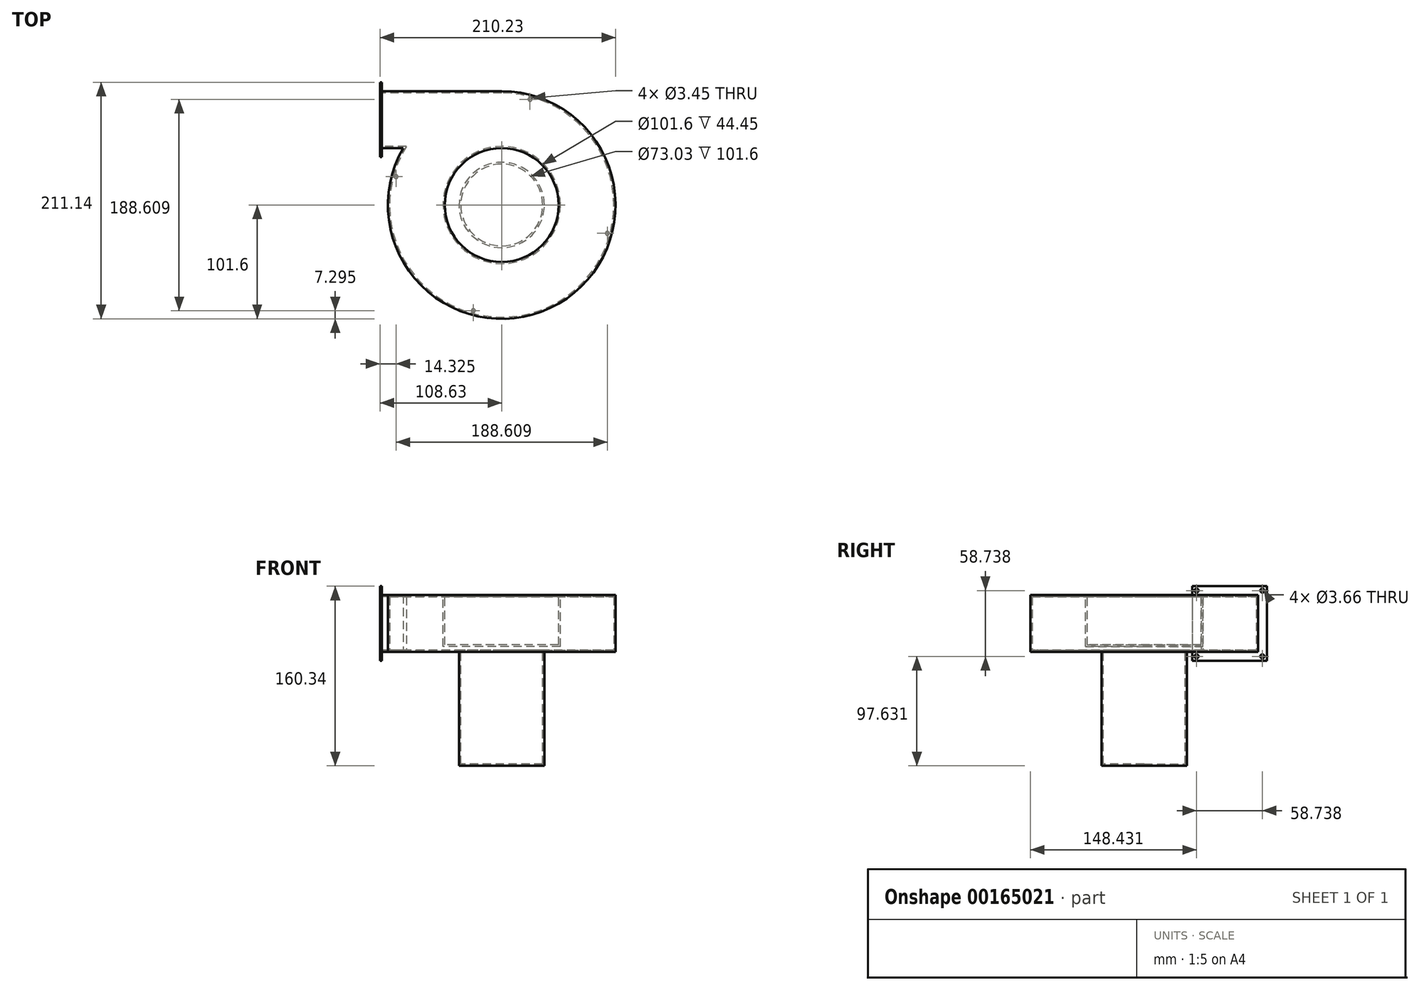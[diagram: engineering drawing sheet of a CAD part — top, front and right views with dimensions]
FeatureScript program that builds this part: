
annotation { "Feature Type Name" : "Feature", "Feature Type Description" : "" }
export const myFeature = defineFeature(function(context is Context, id is Id, definition is map)
    precondition{}
    {
        {
            var Q0;
            Q0=qCreatedBy(makeId("Top.planeOp"),FACE);
            var sketch = newSketch(context, id + "F0", { "sketchPlane" : qUnion([Q0])});
            skLineSegment(sketch, "E0.bottom", {"start": v(-87.99, 50.8) * mm, "end": v(-107.04, 50.8) * mm});
            skLineSegment(sketch, "E0.top", {"start": v(0, 101.6) * mm, "end": v(-107.04, 101.6) * mm});
            skLineSegment(sketch, "E1.top", {"start": v(-107.04, 42.86) * mm, "end": v(-108.63, 42.86) * mm});
            skLineSegment(sketch, "E1.left", {"start": v(-107.04, 50.8) * mm, "end": v(-107.04, 42.86) * mm});
            skLineSegment(sketch, "E2.top", {"start": v(-107.04, 109.54) * mm, "end": v(-108.63, 109.54) * mm});
            skLineSegment(sketch, "E2.left", {"start": v(-107.04, 101.6) * mm, "end": v(-107.04, 109.54) * mm});
            skLineSegment(sketch, "E3", {"start": v(-108.63, 109.54) * mm, "end": v(-108.63, 42.86) * mm});
            skLineSegment(sketch, "E4", {"start": v(-107.04, 50.8) * mm, "end": v(-107.04, 101.6) * mm, "construction": true});
            skArc(sketch, "E5", {"start": v(-87.99, 50.8) * mm, "mid": v(50.8, -87.99) * mm, "end": v(0, 101.6) * mm});
            skSolve(sketch);
        }
        {
            var Q0;
            Q0=makeQuery(id+"F0.imprint","IMPRINT",FACE,{"disambiguationData":[TD([[makeQuery(id+"F0.imprint","IMPRINT",EDGE,{"derivedFrom":sQuery(id+"F0.wireOp",EDGE,"E0.bottom")}),-1.0]])]});
            extrude(context, id + "F1", {"entities" : qUnion([Q0]), "depth" : 50.8 * mm});
        }
        {
            var Q0;
            Q0=makeQuery(id+"F1.opExtrude","CAP_FACE",FACE,{"disambiguationData":[OSD([sQuery(id+"F0.wireOp",EDGE,"E0.bottom"),sQuery(id+"F0.wireOp",EDGE,"E0.top"),sQuery(id+"F0.wireOp",EDGE,"E1.top"),sQuery(id+"F0.wireOp",EDGE,"E1.left"),sQuery(id+"F0.wireOp",EDGE,"E2.top"),sQuery(id+"F0.wireOp",EDGE,"E2.left"),sQuery(id+"F0.wireOp",EDGE,"E3"),sQuery(id+"F0.wireOp",EDGE,"E5")])],"isStart":false});
            var sketch = newSketch(context, id + "F2", { "sketchPlane" : qUnion([Q0])});
            skCircle(sketch, "E6", {"center": v(0, 0) * mm, "radius": 50.8 * mm});
            skSolve(sketch);
        }
        {
            var Q0;
            Q0=qSketchRegion(id+"F2",true);
            extrude(context, id + "F3", {"entities" : qUnion([Q0]), "operationType" : NewBodyOperationType.REMOVE, "oppositeDirection" : true, "depth" : 44.45 * mm});
        }
        {
            var Q0;
            Q0=makeQuery(id+"F1.opExtrude","CAP_FACE",FACE,{"disambiguationData":[OSD([sQuery(id+"F0.wireOp",EDGE,"E0.bottom"),sQuery(id+"F0.wireOp",EDGE,"E0.top"),sQuery(id+"F0.wireOp",EDGE,"E1.top"),sQuery(id+"F0.wireOp",EDGE,"E1.left"),sQuery(id+"F0.wireOp",EDGE,"E2.top"),sQuery(id+"F0.wireOp",EDGE,"E2.left"),sQuery(id+"F0.wireOp",EDGE,"E3"),sQuery(id+"F0.wireOp",EDGE,"E5")])],"isStart":true});
            var sketch = newSketch(context, id + "F4", { "sketchPlane" : qUnion([Q0])});
            skCircle(sketch, "E7", {"center": v(0, 0) * mm, "radius": 38.1 * mm});
            skSolve(sketch);
        }
        {
            var Q0;
            Q0=makeQuery(id+"F4.imprint","IMPRINT",FACE,{"disambiguationData":[TD([[makeQuery(id+"F4.imprint","IMPRINT",EDGE,{"derivedFrom":sQuery(id+"F4.wireOp",EDGE,"E7")}),1.0]])]});
            extrude(context, id + "F5", {"entities" : qUnion([Q0]), "operationType" : NewBodyOperationType.ADD, "depth" : 101.6 * mm});
        }
        {
            var Q0;
            Q0=makeQuery(id+"F1.opExtrude","SWEPT_FACE",FACE,{"disambiguationData":[OSD([sQuery(id+"F0.wireOp",EDGE,"E3")])]});
            shell(context, id + "F6", {"entities" : qUnion([Q0]), "thickness" : 1.59 * mm});
        }
        {
            var Q0;
            Q0=makeQuery(id+"F1.opExtrude","SWEPT_FACE",FACE,{"disambiguationData":[OSD([sQuery(id+"F0.wireOp",EDGE,"E3")])]});
            var sketch = newSketch(context, id + "F7", { "sketchPlane" : qUnion([Q0])});
            skLineSegment(sketch, "E8.bottom", {"start": v(-100.01, 49.21) * mm, "end": v(-52.39, 49.21) * mm});
            skLineSegment(sketch, "E8.top", {"start": v(-100.01, 1.59) * mm, "end": v(-52.39, 1.59) * mm});
            skLineSegment(sketch, "E8.left", {"start": v(-100.01, 49.21) * mm, "end": v(-100.01, 1.59) * mm});
            skLineSegment(sketch, "E8.right", {"start": v(-52.39, 49.21) * mm, "end": v(-52.39, 1.59) * mm});
            skPoint(sketch, "E8.middle", {"position": v(-76.2, 25.4) * mm});
            skLineSegment(sketch, "E9.bottom", {"start": v(-42.86, 58.74) * mm, "end": v(-109.54, 58.74) * mm});
            skLineSegment(sketch, "E9.top", {"start": v(-42.86, -7.94) * mm, "end": v(-109.54, -7.94) * mm});
            skLineSegment(sketch, "E9.left", {"start": v(-42.86, 58.74) * mm, "end": v(-42.86, -7.94) * mm});
            skLineSegment(sketch, "E9.right", {"start": v(-109.54, 58.74) * mm, "end": v(-109.54, -7.94) * mm});
            skSolve(sketch);
        }
        {
            var Q0;
            Q0=qSketchRegion(id+"F7",true);
            var Q1;
            Q1=makeQuery(id+"F1.opExtrude","SWEPT_FACE",FACE,{"disambiguationData":[OSD([sQuery(id+"F0.wireOp",EDGE,"E2.left")])]});
            extrude(context, id + "F8", {"entities" : qUnion([Q0]), "operationType" : NewBodyOperationType.ADD, "endBound" : BoundingType.UP_TO_SURFACE, "oppositeDirection" : true, "endBoundEntityFace" : qUnion([Q1]), "depth" : 25.4 * mm});
        }
        {
            var Q0;
            Q0=makeQuery(id+"F1.opExtrude","SWEPT_FACE",FACE,{"disambiguationData":[OSD([sQuery(id+"F0.wireOp",EDGE,"E3")])]});
            var sketch = newSketch(context, id + "F9", { "sketchPlane" : qUnion([Q0])});
            skLineSegment(sketch, "E10", {"start": v(-76.2, 49.21) * mm, "end": v(-76.2, 1.59) * mm, "construction": true});
            skLineSegment(sketch, "E11.bottom", {"start": v(-105.57, 58.74) * mm, "end": v(-109.54, 58.74) * mm, "construction": true});
            skLineSegment(sketch, "E11.top", {"start": v(-105.57, 54.77) * mm, "end": v(-109.54, 54.77) * mm, "construction": true});
            skLineSegment(sketch, "E11.left", {"start": v(-105.57, 58.74) * mm, "end": v(-105.57, 54.77) * mm, "construction": true});
            skLineSegment(sketch, "E11.right", {"start": v(-109.54, 58.74) * mm, "end": v(-109.54, 54.77) * mm, "construction": true});
            skLineSegment(sketch, "E12.bottom", {"start": v(-105.57, 54.77) * mm, "end": v(-46.83, 54.77) * mm, "construction": true});
            skLineSegment(sketch, "E12.top", {"start": v(-105.57, -3.97) * mm, "end": v(-46.83, -3.97) * mm, "construction": true});
            skLineSegment(sketch, "E12.left", {"start": v(-105.57, 54.77) * mm, "end": v(-105.57, -3.97) * mm, "construction": true});
            skLineSegment(sketch, "E12.right", {"start": v(-46.83, 54.77) * mm, "end": v(-46.83, -3.97) * mm, "construction": true});
            skPoint(sketch, "E12.middle", {"position": v(-76.2, 25.4) * mm});
            skCircle(sketch, "E13", {"center": v(-105.57, 54.77) * mm, "radius": 1.83 * mm});
            skCircle(sketch, "E14", {"center": v(-46.83, 54.77) * mm, "radius": 1.83 * mm});
            skCircle(sketch, "E15", {"center": v(-46.83, -3.97) * mm, "radius": 1.83 * mm});
            skCircle(sketch, "E16", {"center": v(-105.57, -3.97) * mm, "radius": 1.83 * mm});
            skSolve(sketch);
        }
        {
            var Q0;
            Q0=qSketchRegion(id+"F9",true);
            var Q1;
            Q1=makeQuery(id+"F1.opExtrude","SWEPT_FACE",FACE,{"disambiguationData":[OSD([sQuery(id+"F0.wireOp",EDGE,"E2.left")])]});
            extrude(context, id + "F10", {"entities" : qUnion([Q0]), "operationType" : NewBodyOperationType.REMOVE, "endBound" : BoundingType.UP_TO_SURFACE, "oppositeDirection" : true, "endBoundEntityFace" : qUnion([Q1]), "depth" : 25.4 * mm});
        }
        {
            var Q0;
            Q0=makeQuery(id+"F1.opExtrude","CAP_FACE",FACE,{"disambiguationData":[OSD([sQuery(id+"F0.wireOp",EDGE,"E0.bottom"),sQuery(id+"F0.wireOp",EDGE,"E0.top"),sQuery(id+"F0.wireOp",EDGE,"E1.top"),sQuery(id+"F0.wireOp",EDGE,"E1.left"),sQuery(id+"F0.wireOp",EDGE,"E2.top"),sQuery(id+"F0.wireOp",EDGE,"E2.left"),sQuery(id+"F0.wireOp",EDGE,"E3"),sQuery(id+"F0.wireOp",EDGE,"E5")])],"isStart":true});
            var sketch = newSketch(context, id + "F11", { "sketchPlane" : qUnion([Q0])});
            skLineSegment(sketch, "E17.bottom", {"start": v(-94.3, -25.27) * mm, "end": v(-25.27, 94.3) * mm, "construction": true});
            skLineSegment(sketch, "E17.top", {"start": v(25.27, -94.3) * mm, "end": v(94.3, 25.27) * mm, "construction": true});
            skLineSegment(sketch, "E17.left", {"start": v(-94.3, -25.27) * mm, "end": v(25.27, -94.3) * mm, "construction": true});
            skLineSegment(sketch, "E17.right", {"start": v(-25.27, 94.3) * mm, "end": v(94.3, 25.27) * mm, "construction": true});
            skPoint(sketch, "E17.middle", {"position": v(0, 0) * mm});
            skCircle(sketch, "E18", {"center": v(-25.27, 94.3) * mm, "radius": 3.97 * mm, "construction": true});
            skArc(sketch, "E19", {"start": v(-87.99, -50.8) * mm, "mid": v(-50.8, -87.99) * mm, "end": v(0, -101.6) * mm, "construction": true});
            skLineSegment(sketch, "E20", {"start": v(0, 0) * mm, "end": v(-34.52, -59.79) * mm, "construction": true});
            skLineSegment(sketch, "E21", {"start": v(-34.52, -59.79) * mm, "end": v(-50.8, -87.99) * mm, "construction": true});
            skCircle(sketch, "E22", {"center": v(25.27, -94.3) * mm, "radius": 1.73 * mm});
            skCircle(sketch, "E23", {"center": v(-94.3, -25.27) * mm, "radius": 1.73 * mm});
            skCircle(sketch, "E24", {"center": v(-25.27, 94.3) * mm, "radius": 1.73 * mm});
            skCircle(sketch, "E25", {"center": v(94.3, 25.27) * mm, "radius": 1.73 * mm});
            skSolve(sketch);
        }
        {
            var Q0;
            Q0=qSketchRegion(id+"F11",true);
            extrude(context, id + "F12", {"entities" : qUnion([Q0]), "operationType" : NewBodyOperationType.REMOVE, "oppositeDirection" : true, "depth" : 12.7 * mm});
        }
    });
